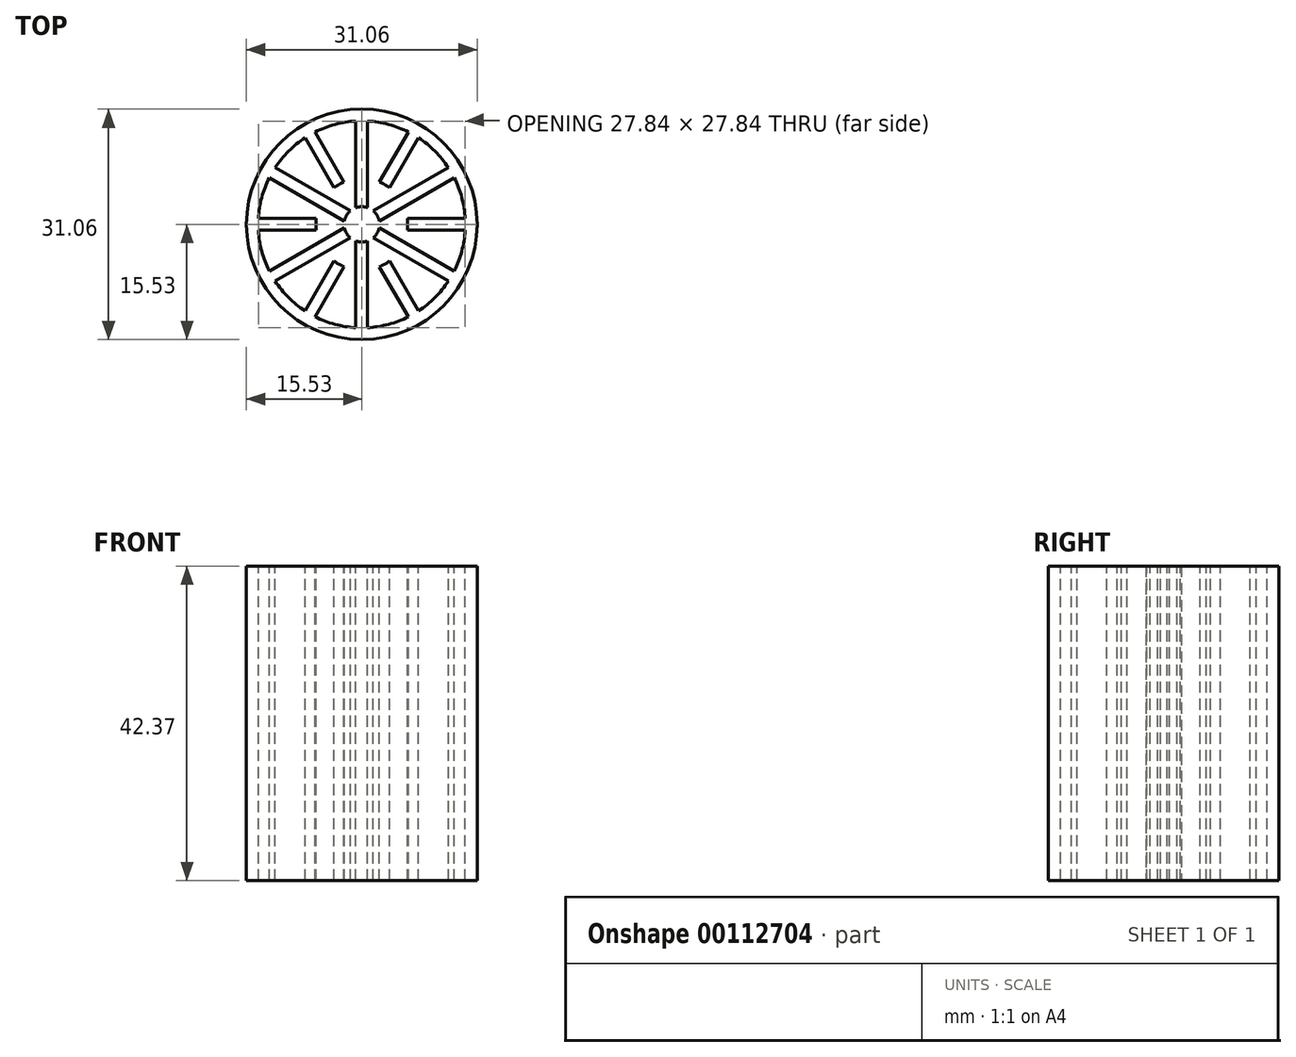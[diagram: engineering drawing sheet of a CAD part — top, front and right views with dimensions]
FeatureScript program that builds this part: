
annotation { "Feature Type Name" : "Feature", "Feature Type Description" : "" }
export const myFeature = defineFeature(function(context is Context, id is Id, definition is map)
    precondition{}
    {
        {
            var Q0;
            Q0=qCreatedBy(makeId("Top.planeOp"),FACE);
            var sketch = newSketch(context, id + "F0", { "sketchPlane" : qUnion([Q0])});
            skCircle(sketch, "E0", {"center": v(0, 0) * mm, "radius": 15.53 * mm});
            skCircle(sketch, "E1", {"center": v(0, 0) * mm, "radius": 2.38 * mm});
            skSolve(sketch);
        }
        {
            var Q0;
            Q0=qSketchRegion(id+"F0",true);
            extrude(context, id + "F1", {"entities" : qUnion([Q0]), "depth" : 42.37 * mm});
        }
        {
            var Q0;
            Q0=makeQuery(id+"F1.opExtrude","CAP_FACE",FACE,{"disambiguationData":[OSD([sQuery(id+"F0.wireOp",EDGE,"E0"),sQuery(id+"F0.wireOp",EDGE,"E1")])],"isStart":false});
            var sketch = newSketch(context, id + "F2", { "sketchPlane" : qUnion([Q0])});
            skLineSegment(sketch, "E2.left", {"start": v(-0.8, 2.25) * mm, "end": v(-0.8, 13.92) * mm});
            skLineSegment(sketch, "E2.right", {"start": v(0.8, 2.25) * mm, "end": v(0.8, 13.92) * mm, "construction": true});
            skArc(sketch, "E3", {"start": v(0.8, 2.25) * mm, "mid": v(0, 2.38) * mm, "end": v(-0.8, 2.25) * mm, "construction": true});
            skLineSegment(sketch, "E4", {"start": v(-0.8, 8.08) * mm, "end": v(0.8, 8.08) * mm, "construction": true});
            skLineSegment(sketch, "E5", {"start": v(0, 0) * mm, "end": v(0, 8.08) * mm, "construction": true});
            skArc(sketch, "E6", {"start": v(0.8, 13.92) * mm, "mid": v(0, 13.94) * mm, "end": v(-0.8, 13.92) * mm, "construction": true});
            skLineSegment(sketch, "E7", {"start": v(0, 0) * mm, "end": v(-7, 4.04) * mm, "construction": true});
            skArc(sketch, "E8", {"start": v(-1.55, 1.8) * mm, "mid": v(-2.06, 1.2) * mm, "end": v(-2.34, 0.44) * mm, "construction": true});
            skLineSegment(sketch, "E9.left", {"start": v(-1.55, 1.8) * mm, "end": v(-11.66, 7.65) * mm});
            skLineSegment(sketch, "E9.right", {"start": v(-2.34, 0.44) * mm, "end": v(-12.45, 6.27) * mm, "construction": true});
            skLineSegment(sketch, "E10", {"start": v(-7.4, 3.35) * mm, "end": v(-6.6, 4.73) * mm, "construction": true});
            skArc(sketch, "E11", {"start": v(-11.66, 7.65) * mm, "mid": v(-12.08, 6.97) * mm, "end": v(-12.45, 6.27) * mm, "construction": true});
            skArc(sketch, "E12", {"start": v(-0.8, 2.25) * mm, "mid": v(-1.2, 2.06) * mm, "end": v(-1.55, 1.8) * mm});
            skLineSegment(sketch, "E13", {"start": v(0, 0) * mm, "end": v(-3.07, 5.32) * mm, "construction": true});
            skPoint(sketch, "E14", {"position": v(-1.2, 2.06) * mm});
            skArc(sketch, "E15", {"start": v(-7.65, 11.66) * mm, "mid": v(-9.86, 9.86) * mm, "end": v(-11.66, 7.65) * mm});
            skLineSegment(sketch, "E16.left", {"start": v(-7.65, 11.66) * mm, "end": v(-3.76, 4.92) * mm});
            skLineSegment(sketch, "E16.right", {"start": v(-6.27, 12.45) * mm, "end": v(-2.38, 5.71) * mm});
            skArc(sketch, "E17", {"start": v(-0.8, 13.92) * mm, "mid": v(-3.6, 13.47) * mm, "end": v(-6.27, 12.45) * mm});
            skLineSegment(sketch, "E18", {"start": v(-2.38, 5.71) * mm, "end": v(-3.76, 4.92) * mm, "construction": true});
            skCircle(sketch, "E19", {"center": v(-2.38, 5.71) * mm, "radius": 1.59 * mm, "construction": true});
            skArc(sketch, "E20", {"start": v(-2.38, 5.71) * mm, "mid": v(-3.1, 5.36) * mm, "end": v(-3.76, 4.92) * mm});
            skSolve(sketch);
        }
        {
            var Q0;
            Q0=qSketchRegion(id+"F2",true);
            var Q1;
            Q1=makeQuery(id+"F1.opExtrude","CAP_FACE",FACE,{"disambiguationData":[OSD([sQuery(id+"F0.wireOp",EDGE,"E0"),sQuery(id+"F0.wireOp",EDGE,"E1")])],"isStart":true});
            extrude(context, id + "F3", {"entities" : qUnion([Q0]), "operationType" : NewBodyOperationType.REMOVE, "endBound" : BoundingType.UP_TO_SURFACE, "oppositeDirection" : true, "endBoundEntityFace" : qUnion([Q1]), "depth" : 25.4 * mm});
        }
        {
            var Q0;
            Q0=makeQuery(id+"F3.boolean.opBoolean","COPY",FACE,{"derivedFrom":makeQuery(id+"F3.opExtrude","SWEPT_FACE",FACE,{"disambiguationData":[OSD([sQuery(id+"F2.wireOp",EDGE,"E9.left")])]})});
            var Q1;
            Q1=makeQuery(id+"F3.boolean.opBoolean","COPY",FACE,{"derivedFrom":makeQuery(id+"F3.opExtrude","SWEPT_FACE",FACE,{"disambiguationData":[OSD([sQuery(id+"F2.wireOp",EDGE,"E15")])]})});
            var Q2;
            Q2=makeQuery(id+"F3.boolean.opBoolean","COPY",FACE,{"derivedFrom":makeQuery(id+"F3.opExtrude","SWEPT_FACE",FACE,{"disambiguationData":[OSD([sQuery(id+"F2.wireOp",EDGE,"E16.left")])]})});
            var Q3;
            Q3=makeQuery(id+"F3.boolean.opBoolean","COPY",FACE,{"derivedFrom":makeQuery(id+"F3.opExtrude","SWEPT_FACE",FACE,{"disambiguationData":[OSD([sQuery(id+"F2.wireOp",EDGE,"E20")])]})});
            var Q4;
            Q4=makeQuery(id+"F3.boolean.opBoolean","COPY",FACE,{"derivedFrom":makeQuery(id+"F3.opExtrude","SWEPT_FACE",FACE,{"disambiguationData":[OSD([sQuery(id+"F2.wireOp",EDGE,"E16.right")])]})});
            var Q5;
            Q5=makeQuery(id+"F3.boolean.opBoolean","COPY",FACE,{"derivedFrom":makeQuery(id+"F3.opExtrude","SWEPT_FACE",FACE,{"disambiguationData":[OSD([sQuery(id+"F2.wireOp",EDGE,"E17")])]})});
            var Q6;
            Q6=makeQuery(id+"F3.boolean.opBoolean","COPY",FACE,{"derivedFrom":makeQuery(id+"F3.opExtrude","SWEPT_FACE",FACE,{"disambiguationData":[OSD([sQuery(id+"F2.wireOp",EDGE,"E2.left")])]})});
            var Q7;
            Q7=makeQuery(id+"F1.opExtrude","SWEPT_FACE",FACE,{"disambiguationData":[OSD([sQuery(id+"F0.wireOp",EDGE,"E1")])]});
            circularPattern(context, id + "F4", {"patternType" : PatternType.FACE, "faces" : qUnion([Q0, Q1, Q2, Q3, Q4, Q5, Q6]), "axis" : qUnion([Q7]), "angle" : 60 * degree, "instanceCount" : 6, "oppositeDirection" : true});
        }
    });
